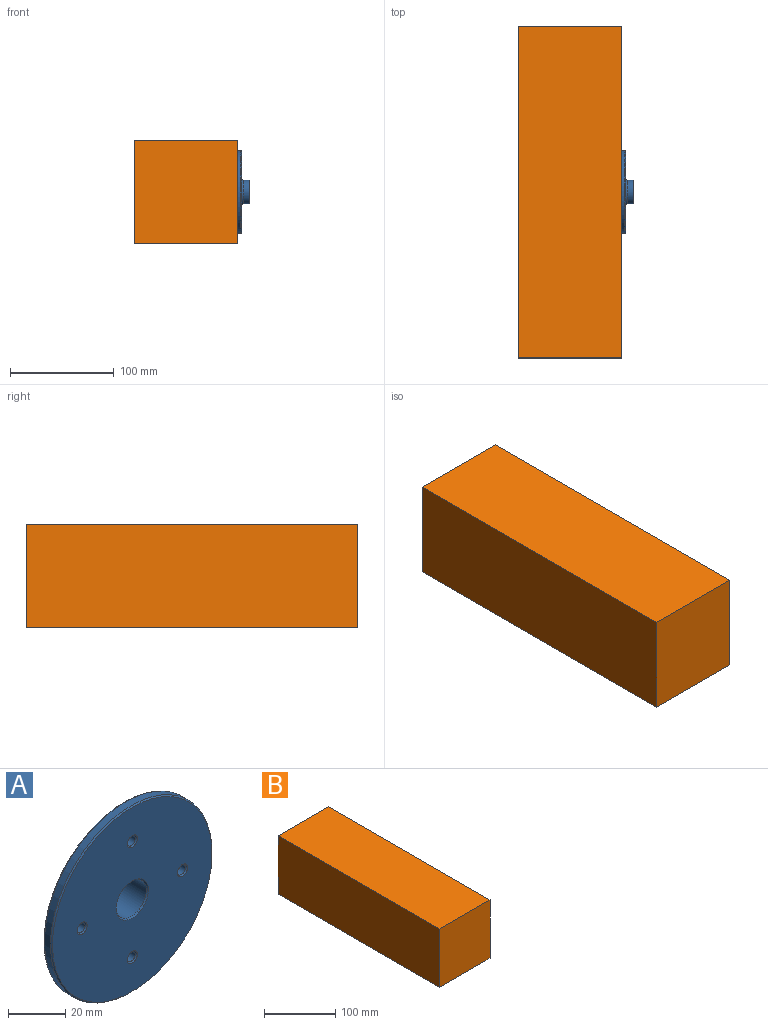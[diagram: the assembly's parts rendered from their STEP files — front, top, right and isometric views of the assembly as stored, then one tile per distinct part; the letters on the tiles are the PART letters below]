
ASSEMBLY  parts=2 mates=1
PART A: 24 faces, bbox 86.6x12x86.6 mm
  f0: torus R=13.5mm, axis (0,1,0), area 241.3mm2, adj f1,f7
  f1: cylinder r=11.5mm len=23mm, axis (0,1,0), area 397.4mm2, adj f0,f9
  f2: plane 22x22mm, normal (0,1,0), area 179.1mm2, adj f8,f9
  f3: cylinder r=7.5mm len=15mm, axis (0,1,0), area 518.4mm2, adj f8,f11
  f4: plane 79x79mm, normal (0,-1,0), area 4622.1mm2, adj f10,f11,f16,f18,f20,f22
  f5: cylinder r=40mm len=80mm, axis (0,1,0), area 754mm2, adj f6,f10
  f6: torus R=39.5mm, axis (0,1,0), area 196.5mm2, adj f5,f7
  f7: plane 79x79mm, normal (0,1,0), area 4250.6mm2, adj f0,f6,f17,f19,f21,f23
  f8: cone r=7.5mm half-angle=45deg, axis (0,1,0), area 34.4mm2, adj f2,f3
  f9: cone r=11mm half-angle=45deg, axis (0,-1,0), area 50mm2, adj f1,f2
  f10: cone r=40mm half-angle=45deg, axis (0,1,0), area 176.6mm2, adj f4,f5
  f11: cone r=8mm half-angle=45deg, axis (0,-1,0), area 34.4mm2, adj f3,f4
  f12: cylinder r=2mm len=4mm, axis (0,1,0), area 37.7mm2, adj f16,f17
  f13: cylinder r=2mm len=4mm, axis (0,1,0), area 37.7mm2, adj f18,f19
  f14: cylinder r=2mm len=4mm, axis (0,1,0), area 37.7mm2, adj f20,f21
  f15: cylinder r=2mm len=4mm, axis (0,1,0), area 37.7mm2, adj f22,f23
  f16: cone r=2mm half-angle=45deg, axis (0,-1,0), area 10mm2, adj f4,f12
  f17: cone r=2mm half-angle=45deg, axis (0,1,0), area 10mm2, adj f7,f12
  f18: cone r=2mm half-angle=45deg, axis (0,-1,0), area 10mm2, adj f4,f13
  f19: cone r=2mm half-angle=45deg, axis (0,1,0), area 10mm2, adj f7,f13
  f20: cone r=2mm half-angle=45deg, axis (0,-1,0), area 10mm2, adj f4,f14
  f21: cone r=2mm half-angle=45deg, axis (0,1,0), area 10mm2, adj f7,f14
  f22: cone r=2mm half-angle=45deg, axis (0,-1,0), area 10mm2, adj f4,f15
  f23: cone r=2mm half-angle=45deg, axis (0,1,0), area 10mm2, adj f7,f15
PART B: 6 faces, bbox 100x320x100 mm
  f0: plane 100x100mm, normal (0,1,0), area 10000mm2, adj f1,f3,f4,f5
  f1: plane 320x100mm, normal (0,0,1), area 32000mm2, adj f0,f2,f3,f4
  f2: plane 100x100mm, normal (0,-1,0), area 10000mm2, adj f1,f3,f4,f5
  f3: plane 320x100mm, normal (1,0,0), area 32000mm2, adj f0,f1,f2,f5
  f4: plane 320x100mm, normal (-1,0,0), area 32000mm2, adj f0,f1,f2,f5
  f5: plane 320x100mm, normal (0,0,-1), area 32000mm2, adj f0,f2,f3,f4
PLACE A rot(axis=(0.58,0.58,-0.58),120deg) t=(59.5,-426.37,1119.43)mm
PLACE B t=(-860,-75.09,-233.57)mm
MATE fastened A.f0 <-> B.f3  axis (1,0,0) through (140,164.91,169.43)mm
